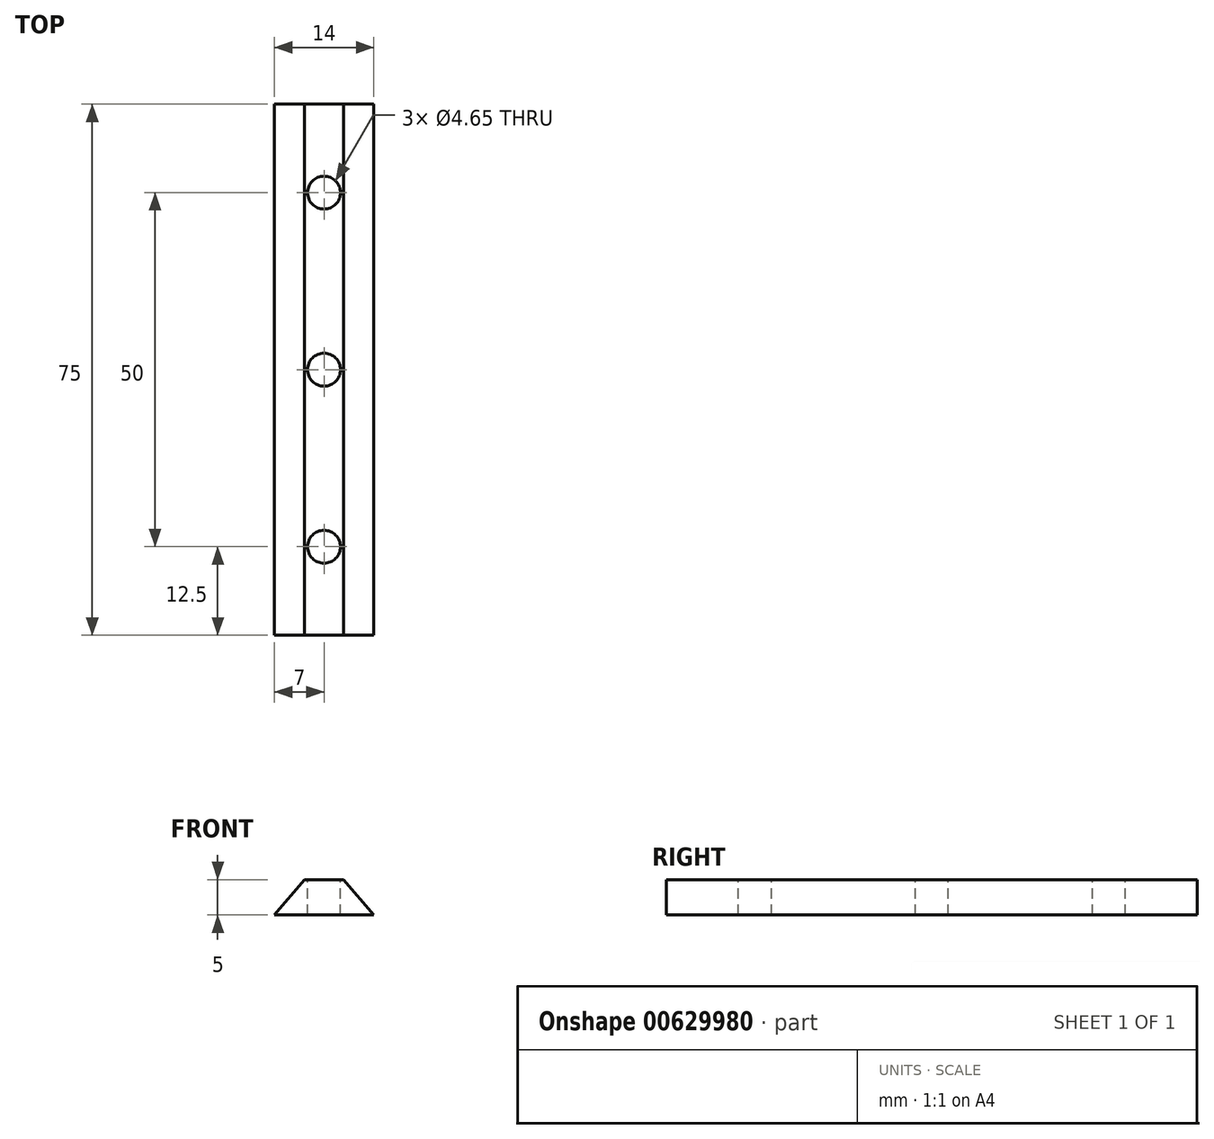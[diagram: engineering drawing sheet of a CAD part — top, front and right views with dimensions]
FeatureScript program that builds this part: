
annotation { "Feature Type Name" : "Feature", "Feature Type Description" : "" }
export const myFeature = defineFeature(function(context is Context, id is Id, definition is map)
    precondition{}
    {
        {
            var Q0;
            Q0=qCreatedBy(makeId("Front.planeOp"),FACE);
            var sketch = newSketch(context, id + "F0", { "sketchPlane" : qUnion([Q0])});
            skLineSegment(sketch, "E0", {"start": v(0, 0) * mm, "end": v(14, 0) * mm});
            skLineSegment(sketch, "E1", {"start": v(4.25, 5) * mm, "end": v(9.75, 5) * mm});
            skLineSegment(sketch, "E2", {"start": v(4.25, 5) * mm, "end": v(0, 0) * mm});
            skLineSegment(sketch, "E3", {"start": v(9.75, 5) * mm, "end": v(14, 0) * mm});
            skLineSegment(sketch, "E4", {"start": v(7, 5) * mm, "end": v(7, 0) * mm});
            skSolve(sketch);
        }
        {
            var Q0;
            Q0 = qSketchRegion(id + "F0", true);
            extrude(context, id + "F1", {"entities" : qUnion([Q0]), "depth" : 75 * mm, "offsetDistance" : 25.4 * mm});
        }
        {
            var Q0;
            Q0=makeQuery(id+"F1.opExtrude","SWEPT_FACE",FACE,{"disambiguationData":[OSD([sQuery(id+"F0.wireOp",EDGE,"E1")])]});
            var sketch = newSketch(context, id + "F2", { "sketchPlane" : qUnion([Q0])});
            skCircle(sketch, "E5", {"center": v(7, -12.5) * mm, "radius": 2.33 * mm});
            skCircle(sketch, "E6", {"center": v(7, -37.5) * mm, "radius": 2.33 * mm});
            skCircle(sketch, "E7", {"center": v(7, -62.5) * mm, "radius": 2.33 * mm});
            skLineSegment(sketch, "E8", {"start": v(7, -75) * mm, "end": v(7, 0) * mm});
            skSolve(sketch);
        }
        {
            var Q0;
            Q0 = qSketchRegion(id + "F2", true);
            extrude(context, id + "F3", {"entities" : qUnion([Q0]), "operationType" : NewBodyOperationType.REMOVE, "endBound" : BoundingType.UP_TO_NEXT, "oppositeDirection" : true, "depth" : 25.4 * mm, "offsetDistance" : 25.4 * mm});
        }
    });
